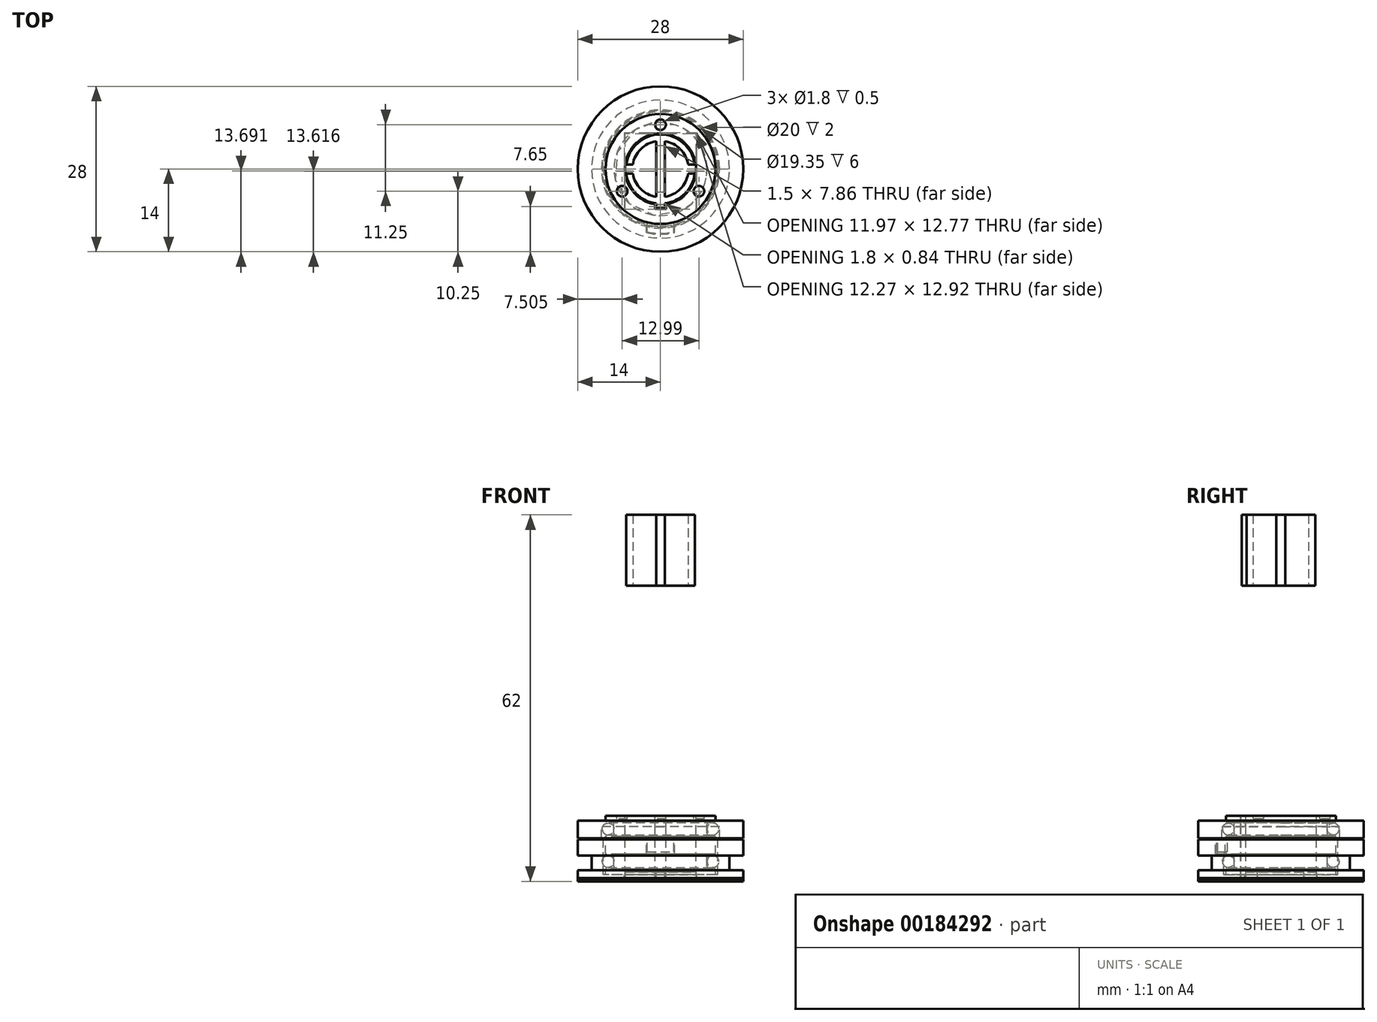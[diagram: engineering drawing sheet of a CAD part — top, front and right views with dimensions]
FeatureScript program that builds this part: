
annotation { "Feature Type Name" : "Feature", "Feature Type Description" : "" }
export const myFeature = defineFeature(function(context is Context, id is Id, definition is map)
    precondition{}
    {
        {
            assignVariable(context, id + "F0", {"name" : "fitT", "anyValue" : .15});
        }
        {
            assignVariable(context, id + "F1", {"name" : "slitWidth", "anyValue" : 1.5});
        }
        {
            assignVariable(context, id + "F2", {"name" : "topTierThick", "anyValue" : 1});
        }
        {
            assignVariable(context, id + "F3", {"name" : "bottomTierThick", "anyValue" : .55});
        }
        {
            assignVariable(context, id + "F4", {"name" : "bottomRingWall", "anyValue" : 6});
        }
        {
            assignVariable(context, id + "F5", {"name" : "oRingDiameter", "anyValue" : 2});
        }
        {
            assignVariable(context, id + "F6", {"name" : "ccThick", "anyValue" : 12});
        }
        {
            var Q0;
            Q0=qCreatedBy(makeId("Top.planeOp"),FACE);
            var sketch = newSketch(context, id + "F7", { "sketchPlane" : qUnion([Q0])});
            skCircle(sketch, "E0", {"center": v(0, 0) * mm, "radius": 14 * mm});
            skSolve(sketch);
        }
        {
            var Q0;
            Q0=makeQuery(id+"F7.imprint","IMPRINT",FACE,{"disambiguationData":[TD([[makeQuery(id+"F7.imprint","IMPRINT",EDGE,{"derivedFrom":sQuery(id+"F7.wireOp",EDGE,"E0")}),1.0]])]});
            extrude(context, id + "F8", {"entities" : qUnion([Q0]), "depth" : (getVariable(context, 'bottomTierThick')) * mm});
        }
        {
            var Q0;
            Q0=makeQuery(id+"F8.opExtrude","CAP_FACE",FACE,{"disambiguationData":[OSD([sQuery(id+"F7.wireOp",EDGE,"E0")])],"isStart":false});
            var sketch = newSketch(context, id + "F9", { "sketchPlane" : qUnion([Q0])});
            skArc(sketch, "E1", {"start": v(0.6, -5.97) * mm, "mid": v(0, 6) * mm, "end": v(-0.6, -5.97) * mm});
            skLineSegment(sketch, "E2", {"start": v(0, 0) * mm, "end": v(0, -14) * mm, "construction": true});
            skLineSegment(sketch, "E3.bottom", {"start": v(0.6, -6.6) * mm, "end": v(-0.6, -6.6) * mm});
            skLineSegment(sketch, "E3.left", {"start": v(0.6, -6.6) * mm, "end": v(0.6, -5.97) * mm});
            skLineSegment(sketch, "E3.right", {"start": v(-0.6, -6.6) * mm, "end": v(-0.6, -5.97) * mm});
            skPoint(sketch, "E3.middle", {"position": v(0, -6) * mm});
            skLineSegment(sketch, "E4", {"start": v(-2.04, -6) * mm, "end": v(2.09, -6) * mm, "construction": true});
            skSolve(sketch);
        }
        {
            var Q0;
            Q0=makeQuery(id+"F9.imprint","IMPRINT",FACE,{"disambiguationData":[TD([[makeQuery(id+"F9.imprint","IMPRINT",EDGE,{"derivedFrom":sQuery(id+"F9.wireOp",EDGE,"E1")}),1.0]])]});
            extrude(context, id + "F10", {"entities" : qUnion([Q0]), "operationType" : NewBodyOperationType.ADD, "depth" : (getVariable(context, 'topTierThick')) * mm});
        }
        {
            var Q0;
            Q0=makeQuery(id+"F10.opExtrude","CAP_FACE",FACE,{"disambiguationData":[OSD([sQuery(id+"F9.wireOp",EDGE,"E1")])],"isStart":false});
            var sketch = newSketch(context, id + "F11", { "sketchPlane" : qUnion([Q0])});
            skPoint(sketch, "E5.rect.middle", {"position": v(0, 0) * mm});
            skCircle(sketch, "E6", {"center": v(0, 0) * mm, "radius": 4 * mm, "construction": true});
            skLineSegment(sketch, "E7.rect.bottom", {"start": v(0.75, 3.93) * mm, "end": v(-0.75, 3.93) * mm});
            skLineSegment(sketch, "E7.rect.top", {"start": v(0.75, -3.93) * mm, "end": v(-0.75, -3.93) * mm});
            skLineSegment(sketch, "E7.rect.left", {"start": v(0.75, 3.93) * mm, "end": v(0.75, -3.93) * mm});
            skLineSegment(sketch, "E7.rect.right", {"start": v(-0.75, 3.93) * mm, "end": v(-0.75, -3.93) * mm});
            skSolve(sketch);
        }
        {
            var Q0;
            Q0=makeQuery(id+"F11.imprint","IMPRINT",FACE,{"disambiguationData":[TD([[makeQuery(id+"F11.imprint","IMPRINT",EDGE,{"derivedFrom":sQuery(id+"F11.wireOp",EDGE,"E7.rect.bottom")}),1.0]])]});
            var Q1;
            Q1=makeQuery(id+"F8.opExtrude","CAP_FACE",FACE,{"disambiguationData":[OSD([sQuery(id+"F7.wireOp",EDGE,"E0")])],"isStart":true});
            extrude(context, id + "F12", {"entities" : qUnion([Q0]), "operationType" : NewBodyOperationType.REMOVE, "endBound" : BoundingType.UP_TO_SURFACE, "oppositeDirection" : true, "endBoundEntityFace" : qUnion([Q1]), "depth" : 25 * mm});
        }
        {
            var Q0;
            Q0=qCreatedBy(makeId("Front.planeOp"),FACE);
            var sketch = newSketch(context, id + "F13", { "sketchPlane" : qUnion([Q0])});
            skLineSegment(sketch, "E8.bottom", {"start": v(-14, 7.1) * mm, "end": v(-9.67, 7.1) * mm});
            skLineSegment(sketch, "E8.top", {"start": v(-14, 0.1) * mm, "end": v(-9.67, 0.1) * mm});
            skLineSegment(sketch, "E8.left", {"start": v(-14, 7.1) * mm, "end": v(-14, 4.35) * mm});
            skLineSegment(sketch, "E8.right", {"start": v(-9.67, 7.1) * mm, "end": v(-9.67, 1.1) * mm});
            skLineSegment(sketch, "E9.bottom", {"start": v(-9.67, 1.1) * mm, "end": v(-6.15, 1.1) * mm});
            skLineSegment(sketch, "E9.top", {"start": v(-14, 0.1) * mm, "end": v(-6.15, 0.1) * mm});
            skLineSegment(sketch, "E9.left", {"start": v(-14, 1.1) * mm, "end": v(-14, 0.1) * mm});
            skLineSegment(sketch, "E9.right", {"start": v(-6.15, 1.1) * mm, "end": v(-6.15, 0.1) * mm});
            skLineSegment(sketch, "E10", {"start": v(0, 8.92) * mm, "end": v(0, -8.7) * mm, "construction": true});
            skLineSegment(sketch, "E11", {"start": v(-12.77, 0) * mm, "end": v(12.68, 0) * mm, "construction": true});
            skLineSegment(sketch, "E12.bottom", {"start": v(-14, 4.35) * mm, "end": v(-11.67, 4.35) * mm});
            skLineSegment(sketch, "E12.top", {"start": v(-14, 1.85) * mm, "end": v(-11.67, 1.85) * mm});
            skLineSegment(sketch, "E12.right", {"start": v(-11.67, 4.35) * mm, "end": v(-11.67, 1.85) * mm});
            skLineSegment(sketch, "E13.trimOffspring", {"start": v(-14, 1.85) * mm, "end": v(-14, 0.1) * mm});
            skSolve(sketch);
        }
        {
            var Q0;
            Q0=makeQuery(id+"F13.imprint","IMPRINT",FACE,{"disambiguationData":[TD([[makeQuery(id+"F13.imprint","IMPRINT",EDGE,{"derivedFrom":sQuery(id+"F13.wireOp",EDGE,"E8.bottom")}),-1.0]])]});
            var Q1;
            Q1=sQuery(id+"F13.wireOp",EDGE,"E10");
            revolve(context, id + "F14", {"entities" : qUnion([Q0]), "axis" : qUnion([Q1]), "revolveType" : RevolveType.FULL});
        }
        {
            var Q0;
            Q0=qCreatedBy(makeId("Front.planeOp"),FACE);
            var sketch = newSketch(context, id + "F15", { "sketchPlane" : qUnion([Q0])});
            skLineSegment(sketch, "E14.bottom", {"start": v(-14, 10.25) * mm, "end": v(0, 10.25) * mm});
            skLineSegment(sketch, "E14.top", {"start": v(-14, 7.25) * mm, "end": v(-10, 7.25) * mm});
            skLineSegment(sketch, "E14.left", {"start": v(-14, 10.25) * mm, "end": v(-14, 7.25) * mm});
            skLineSegment(sketch, "E14.right", {"start": v(0, 10.25) * mm, "end": v(0, 9.25) * mm});
            skLineSegment(sketch, "E15.top", {"start": v(-10, 9.25) * mm, "end": v(0, 9.25) * mm});
            skLineSegment(sketch, "E15.left", {"start": v(-10, 7.25) * mm, "end": v(-10, 9.25) * mm});
            skSolve(sketch);
        }
        {
            var Q0;
            Q0=makeQuery(id+"F15.imprint","IMPRINT",FACE,{"disambiguationData":[TD([[makeQuery(id+"F15.imprint","IMPRINT",EDGE,{"derivedFrom":sQuery(id+"F15.wireOp",EDGE,"E14.bottom")}),-1.0]])]});
            var Q1;
            Q1=sQuery(id+"F13.wireOp",EDGE,"E10");
            revolve(context, id + "F16", {"entities" : qUnion([Q0]), "axis" : qUnion([Q1]), "revolveType" : RevolveType.FULL});
        }
        {
            var Q0;
            Q0=qCreatedBy(makeId("Top.planeOp"),FACE);
            cPlane(context, id + "F17", {"entities" : qUnion([Q0]), "cplaneType" : CPlaneType.OFFSET, "offset" : 50 * mm, "width" : 150 * mm, "height" : 150 * mm});
        }
        {
            var Q0;
            Q0=qCreatedBy(id+"F17.planeOp",FACE);
            var sketch = newSketch(context, id + "F18", { "sketchPlane" : qUnion([Q0])});
            skArc(sketch, "E16", {"start": v(-5.8, -0.75) * mm, "mid": v(0, -5.85) * mm, "end": v(5.8, -0.75) * mm});
            skArc(sketch, "E17", {"start": v(4.7, 0.75) * mm, "mid": v(3.36, 3.36) * mm, "end": v(0.75, 4.7) * mm});
            skLineSegment(sketch, "E18.left", {"start": v(-0.75, 4.7) * mm, "end": v(-0.75, -4.7) * mm});
            skLineSegment(sketch, "E18.right", {"start": v(0.75, 4.7) * mm, "end": v(0.75, -4.7) * mm});
            skLineSegment(sketch, "E19.bottom", {"start": v(-5.8, 0.75) * mm, "end": v(-4.7, 0.75) * mm});
            skLineSegment(sketch, "E19.top", {"start": v(-5.8, -0.75) * mm, "end": v(-4.7, -0.75) * mm});
            skArc(sketch, "E20.trimOffspring", {"start": v(5.8, 0.75) * mm, "mid": v(0, 5.85) * mm, "end": v(-5.8, 0.75) * mm});
            skArc(sketch, "E21.trimOffspring", {"start": v(-4.7, -0.75) * mm, "mid": v(-3.36, -3.36) * mm, "end": v(-0.75, -4.7) * mm});
            skLineSegment(sketch, "E22.trimOffspring", {"start": v(4.7, 0.75) * mm, "end": v(5.8, 0.75) * mm});
            skArc(sketch, "E23.trimOffspring", {"start": v(-0.75, 4.7) * mm, "mid": v(-3.36, 3.36) * mm, "end": v(-4.7, 0.75) * mm});
            skLineSegment(sketch, "E24.trimOffspring", {"start": v(4.7, -0.75) * mm, "end": v(5.8, -0.75) * mm});
            skArc(sketch, "E25.trimOffspring", {"start": v(0.75, -4.7) * mm, "mid": v(3.36, -3.36) * mm, "end": v(4.7, -0.75) * mm});
            skSolve(sketch);
        }
        {
            var Q0;
            Q0=qSketchRegion(id+"F18",true);
            extrude(context, id + "F19", {"entities" : qUnion([Q0]), "depth" : (getVariable(context, 'ccThick')) * mm});
        }
        {
            var Q0;
            Q0=qCreatedBy(makeId("Front.planeOp"),FACE);
            var sketch = newSketch(context, id + "F20", { "sketchPlane" : qUnion([Q0])});
            skLineSegment(sketch, "E26.bottom", {"start": v(-9.3, 11.1) * mm, "end": v(-6, 11.1) * mm});
            skLineSegment(sketch, "E26.top", {"start": v(-9.3, 1.1) * mm, "end": v(-6, 1.1) * mm});
            skLineSegment(sketch, "E26.left", {"start": v(-9.3, 11.1) * mm, "end": v(-9.3, 10.1) * mm});
            skLineSegment(sketch, "E26.right", {"start": v(-6, 11.1) * mm, "end": v(-6, 1.1) * mm});
            skLineSegment(sketch, "E27.bottom", {"start": v(-9.3, 4.6) * mm, "end": v(-8.38, 4.6) * mm});
            skLineSegment(sketch, "E27.top", {"start": v(-9.3, 2.1) * mm, "end": v(-8.38, 2.1) * mm});
            skLineSegment(sketch, "E27.right", {"start": v(-7.87, 4.1) * mm, "end": v(-7.87, 2.6) * mm});
            skLineSegment(sketch, "E28.bottom", {"start": v(-9.3, 10.1) * mm, "end": v(-8.38, 10.1) * mm});
            skLineSegment(sketch, "E28.top", {"start": v(-9.3, 7.6) * mm, "end": v(-8.38, 7.6) * mm});
            skLineSegment(sketch, "E28.right", {"start": v(-7.88, 9.6) * mm, "end": v(-7.88, 8.1) * mm});
            skLineSegment(sketch, "E29.trimOffspring", {"start": v(-9.3, 7.6) * mm, "end": v(-9.3, 4.6) * mm});
            skLineSegment(sketch, "E30.trimOffspring", {"start": v(-9.3, 2.1) * mm, "end": v(-9.3, 1.1) * mm});
            skPoint(sketch, "E31.visualSharp", {"position": v(-7.88, 10.1) * mm});
            skArc(sketch, "E31.filletArc", {"start": v(-7.88, 9.6) * mm, "mid": v(-8.02, 9.95) * mm, "end": v(-8.38, 10.1) * mm});
            skPoint(sketch, "E32.visualSharp", {"position": v(-7.88, 7.6) * mm});
            skArc(sketch, "E32.filletArc", {"start": v(-8.38, 7.6) * mm, "mid": v(-8.02, 7.75) * mm, "end": v(-7.88, 8.1) * mm});
            skPoint(sketch, "E33.visualSharp", {"position": v(-7.88, 4.6) * mm});
            skArc(sketch, "E33.filletArc", {"start": v(-7.88, 4.1) * mm, "mid": v(-8.02, 4.45) * mm, "end": v(-8.38, 4.6) * mm});
            skPoint(sketch, "E34.visualSharp", {"position": v(-7.88, 2.1) * mm});
            skArc(sketch, "E34.filletArc", {"start": v(-8.38, 2.1) * mm, "mid": v(-8.02, 2.25) * mm, "end": v(-7.88, 2.6) * mm});
            skLineSegment(sketch, "E35", {"start": v(-7.88, 8.1) * mm, "end": v(-7.88, 4.1) * mm, "construction": true});
            skPoint(sketch, "E36", {"position": v(-7.88, 8.85) * mm});
            skPoint(sketch, "E37", {"position": v(-7.88, 3.35) * mm});
            skCircle(sketch, "E38", {"center": v(-8.88, 3.35) * mm, "radius": 1 * mm});
            skCircle(sketch, "E39", {"center": v(-8.88, 8.85) * mm, "radius": 1 * mm});
            skLineSegment(sketch, "E40", {"start": v(0, 21.5) * mm, "end": v(0, -11.55) * mm, "construction": true});
            skSolve(sketch);
        }
        {
            var Q0;
            Q0=makeQuery(id+"F20.imprint","IMPRINT",FACE,{"disambiguationData":[TD([[makeQuery(id+"F20.imprint","IMPRINT",EDGE,{"derivedFrom":sQuery(id+"F20.wireOp",EDGE,"E26.bottom")}),-1.0]])]});
            var Q1;
            Q1=sQuery(id+"F20.wireOp",EDGE,"E40");
            revolve(context, id + "F21", {"entities" : qUnion([Q0]), "axis" : qUnion([Q1]), "revolveType" : RevolveType.FULL});
        }
        {
            var Q0;
            Q0=makeQuery(id+"F20.imprint","IMPRINT",FACE,{"disambiguationData":[TD([[makeQuery(id+"F20.imprint","IMPRINT",EDGE,{"derivedFrom":sQuery(id+"F20.wireOp",EDGE,"E39")}),1.0]])]});
            var Q1;
            Q1=makeQuery(id+"F20.imprint","IMPRINT",FACE,{"disambiguationData":[TD([[makeQuery(id+"F20.imprint","IMPRINT",EDGE,{"derivedFrom":sQuery(id+"F20.wireOp",EDGE,"E38")}),1.0]])]});
            var Q2;
            Q2=sQuery(id+"F20.wireOp",EDGE,"E40");
            revolve(context, id + "F22", {"entities" : qUnion([Q0, Q1]), "axis" : qUnion([Q2]), "revolveType" : RevolveType.FULL});
        }
        {
            var Q0;
            Q0=makeQuery(id+"F14.opRevolve","SWEPT_FACE",FACE,{"disambiguationData":[OSD([sQuery(id+"F13.wireOp",EDGE,"E8.bottom")])]});
            var sketch = newSketch(context, id + "F23", { "sketchPlane" : qUnion([Q0])});
            skLineSegment(sketch, "E41", {"start": v(0, 14) * mm, "end": v(0, -14) * mm, "construction": true});
            skLineSegment(sketch, "E42", {"start": v(0, -14) * mm, "end": v(14, 0) * mm, "construction": true});
            skLineSegment(sketch, "E43", {"start": v(14, 0) * mm, "end": v(-14, 0) * mm, "construction": true});
            skLineSegment(sketch, "E44", {"start": v(-14, 0) * mm, "end": v(0, -14) * mm, "construction": true});
            skLineSegment(sketch, "E45", {"start": v(0, 14) * mm, "end": v(-14, 0) * mm, "construction": true});
            skLineSegment(sketch, "E46", {"start": v(14, 0) * mm, "end": v(0, 14) * mm, "construction": true});
            skLineSegment(sketch, "E47.left", {"start": v(2.4, -10.76) * mm, "end": v(2.4, -9.37) * mm});
            skLineSegment(sketch, "E47.right", {"start": v(-2.4, -10.76) * mm, "end": v(-2.4, -9.37) * mm});
            skPoint(sketch, "E47.middle", {"position": v(0, -7.24) * mm});
            skArc(sketch, "E48", {"start": v(-2.4, -9.37) * mm, "mid": v(0, -9.68) * mm, "end": v(2.4, -9.37) * mm});
            skPoint(sketch, "E49.orphan", {"position": v(2.4, -3.72) * mm});
            skPoint(sketch, "E47.top.end.orphan", {"position": v(-2.4, -3.72) * mm});
            skArc(sketch, "E50", {"start": v(-2.4, -10.76) * mm, "mid": v(0, -11.03) * mm, "end": v(2.4, -10.76) * mm});
            skSolve(sketch);
        }
        {
            var Q0;
            Q0=makeQuery(id+"F23.imprint","IMPRINT",FACE,{"disambiguationData":[TD([[makeQuery(id+"F23.imprint","IMPRINT",EDGE,{"derivedFrom":sQuery(id+"F23.wireOp",EDGE,"E47.left")}),1.0]])]});
            extrude(context, id + "F24", {"entities" : qUnion([Q0]), "operationType" : NewBodyOperationType.REMOVE, "oppositeDirection" : true, "depth" : (3 / 2 * getVariable(context, 'slitWidth') + getVariable(context, 'fitT')) * mm});
        }
        {
            var Q0;
            Q0=makeQuery(id+"F14.opRevolve","SWEPT_FACE",FACE,{"disambiguationData":[OSD([sQuery(id+"F13.wireOp",EDGE,"E8.bottom")])]});
            var sketch = newSketch(context, id + "F25", { "sketchPlane" : qUnion([Q0])});
            skArc(sketch, "E51", {"start": v(-2.25, -10.64) * mm, "mid": v(0, -10.88) * mm, "end": v(2.25, -10.64) * mm});
            skLineSegment(sketch, "E52", {"start": v(10.42, 0) * mm, "end": v(-10.42, 0) * mm, "construction": true});
            skLineSegment(sketch, "E53", {"start": v(0, -10.88) * mm, "end": v(0, 10.88) * mm, "construction": true});
            skPoint(sketch, "E53.endSnap0", {"position": v(0, 9.67) * mm});
            skLineSegment(sketch, "E54.left", {"start": v(2.25, -10.64) * mm, "end": v(2.25, -5.56) * mm});
            skLineSegment(sketch, "E54.right", {"start": v(-2.25, -10.64) * mm, "end": v(-2.25, -5.56) * mm});
            skPoint(sketch, "E54.middle", {"position": v(0, -7.65) * mm});
            skArc(sketch, "E55", {"start": v(-2.25, -5.56) * mm, "mid": v(0, -6) * mm, "end": v(2.25, -5.56) * mm});
            skPoint(sketch, "E56.orphan", {"position": v(2.25, -4.67) * mm});
            skPoint(sketch, "E57.orphan", {"position": v(-2.25, -4.67) * mm});
            skSolve(sketch);
        }
        {
            var Q0;
            {var subQ1=sQuery(id+"F25.wireOp",EDGE,"E51");Q0=makeQuery(id+"F25.imprint","IMPRINT",FACE,{"disambiguationData":[TD([[makeQuery(id+"F25.imprint","IMPRINT",EDGE,{"derivedFrom":subQ1}),1.0]])]});}
            var Q1;
            {var subQ0=sQuery(id+"F25.wireOp",EDGE,"E55");Q1=makeQuery(id+"F25.imprint","IMPRINT",FACE,{"disambiguationData":[TD([[makeQuery(id+"F25.imprint","IMPRINT",EDGE,{"derivedFrom":subQ0}),-1.0]])]});}
            extrude(context, id + "F26", {"entities" : qUnion([Q0, Q1]), "operationType" : NewBodyOperationType.ADD, "oppositeDirection" : true, "depth" : (3 / 2 * getVariable(context, 'slitWidth') - getVariable(context, 'fitT')) * mm});
        }
        {
            var Q0;
            Q0=makeQuery(id+"F21.opRevolve","SWEPT_FACE",FACE,{"disambiguationData":[OSD([sQuery(id+"F20.wireOp",EDGE,"E26.bottom")])]});
            var sketch = newSketch(context, id + "F27", { "sketchPlane" : qUnion([Q0])});
            skLineSegment(sketch, "E58", {"start": v(0, 9.3) * mm, "end": v(0, -9.3) * mm, "construction": true});
            skLineSegment(sketch, "E59", {"start": v(0, -9.3) * mm, "end": v(9.3, 0) * mm, "construction": true});
            skLineSegment(sketch, "E60", {"start": v(9.3, 0) * mm, "end": v(-9.3, 0) * mm, "construction": true});
            skLineSegment(sketch, "E61", {"start": v(-9.3, 0) * mm, "end": v(0, 9.3) * mm, "construction": true});
            skLineSegment(sketch, "E62", {"start": v(0, 9.3) * mm, "end": v(9.3, 0) * mm, "construction": true});
            skLineSegment(sketch, "E63", {"start": v(0, -9.3) * mm, "end": v(-9.3, 0) * mm, "construction": true});
            skLineSegment(sketch, "E64.bottom", {"start": v(0.9, -6.77) * mm, "end": v(-0.9, -6.73) * mm});
            skLineSegment(sketch, "E64.left", {"start": v(0.9, -6.77) * mm, "end": v(0.9, -5.93) * mm});
            skLineSegment(sketch, "E64.right", {"start": v(-0.9, -6.73) * mm, "end": v(-0.9, -5.93) * mm});
            skPoint(sketch, "E64.middle", {"position": v(0, -6) * mm});
            skArc(sketch, "E65", {"start": v(-0.9, -5.93) * mm, "mid": v(0, -6) * mm, "end": v(0.9, -5.93) * mm});
            skPoint(sketch, "E66.orphan", {"position": v(-0.9, -5.23) * mm});
            skPoint(sketch, "E67.orphan", {"position": v(0.9, -5.27) * mm});
            skLineSegment(sketch, "E68", {"start": v(-3.37, -5.93) * mm, "end": v(3.24, -6.07) * mm, "construction": true});
            skSolve(sketch);
        }
        {
            var Q0;
            Q0=makeQuery(id+"F27.imprint","IMPRINT",FACE,{"disambiguationData":[TD([[makeQuery(id+"F27.imprint","IMPRINT",EDGE,{"derivedFrom":sQuery(id+"F27.wireOp",EDGE,"E64.bottom")}),-1.0]])]});
            var Q1;
            Q1=makeQuery(id+"F14.opRevolve","SWEPT_FACE",FACE,{"disambiguationData":[OSD([sQuery(id+"F13.wireOp",EDGE,"E9.top")])]});
            extrude(context, id + "F28", {"entities" : qUnion([Q0]), "operationType" : NewBodyOperationType.REMOVE, "endBound" : BoundingType.UP_TO_SURFACE, "oppositeDirection" : true, "endBoundEntityFace" : qUnion([Q1]), "depth" : (getVariable(context, 'bottomRingWall') + 2 * getVariable(context, 'oRingDiameter')) * mm});
        }
        {
            var Q0;
            Q0=makeQuery(id+"F19.opExtrude","CAP_FACE",FACE,{"disambiguationData":[OSD([sQuery(id+"F18.wireOp",EDGE,"E16"),sQuery(id+"F18.wireOp",EDGE,"E17"),sQuery(id+"F18.wireOp",EDGE,"E18.left"),sQuery(id+"F18.wireOp",EDGE,"E18.right"),sQuery(id+"F18.wireOp",EDGE,"E19.bottom"),sQuery(id+"F18.wireOp",EDGE,"E19.top"),sQuery(id+"F18.wireOp",EDGE,"E20.trimOffspring"),sQuery(id+"F18.wireOp",EDGE,"E21.trimOffspring"),sQuery(id+"F18.wireOp",EDGE,"E22.trimOffspring"),sQuery(id+"F18.wireOp",EDGE,"E23.trimOffspring"),sQuery(id+"F18.wireOp",EDGE,"E24.trimOffspring"),sQuery(id+"F18.wireOp",EDGE,"E25.trimOffspring")])],"isStart":false});
            var sketch = newSketch(context, id + "F29", { "sketchPlane" : qUnion([Q0])});
            skLineSegment(sketch, "E69", {"start": v(0, 5.85) * mm, "end": v(0, -5.85) * mm, "construction": true});
            skLineSegment(sketch, "E70", {"start": v(0, -5.85) * mm, "end": v(5.8, 0) * mm, "construction": true});
            skLineSegment(sketch, "E71", {"start": v(5.8, 0) * mm, "end": v(-5.8, 0) * mm, "construction": true});
            skLineSegment(sketch, "E72", {"start": v(-5.8, 0) * mm, "end": v(0, 5.85) * mm, "construction": true});
            skLineSegment(sketch, "E73", {"start": v(5.8, 0) * mm, "end": v(0, 5.85) * mm, "construction": true});
            skLineSegment(sketch, "E74", {"start": v(0, -5.85) * mm, "end": v(-5.8, 0) * mm, "construction": true});
            skLineSegment(sketch, "E75.bottom", {"start": v(0.75, -6.6) * mm, "end": v(-0.75, -6.6) * mm});
            skLineSegment(sketch, "E75.top", {"start": v(0.75, -5.1) * mm, "end": v(-0.75, -5.1) * mm});
            skLineSegment(sketch, "E75.left", {"start": v(0.75, -6.6) * mm, "end": v(0.75, -5.1) * mm});
            skLineSegment(sketch, "E75.right", {"start": v(-0.75, -6.6) * mm, "end": v(-0.75, -5.1) * mm});
            skPoint(sketch, "E75.middle", {"position": v(0, -5.85) * mm});
            skSolve(sketch);
        }
        {
            var Q0;
            {var subQ0=sQuery(id+"F29.wireOp",EDGE,"E75.bottom");Q0=makeQuery(id+"F29.imprint","IMPRINT",FACE,{"disambiguationData":[TD([[makeQuery(id+"F29.imprint","IMPRINT",EDGE,{"derivedFrom":subQ0}),-1.0]])]});}
            extrude(context, id + "F30", {"entities" : qUnion([Q0]), "operationType" : NewBodyOperationType.ADD, "oppositeDirection" : true, "depth" : (getVariable(context, 'ccThick')) * mm});
        }
        {
            var Q0;
            Q0=makeQuery(id+"F21.opRevolve","SWEPT_FACE",FACE,{"disambiguationData":[OSD([sQuery(id+"F20.wireOp",EDGE,"E26.bottom")])]});
            var sketch = newSketch(context, id + "F31", { "sketchPlane" : qUnion([Q0])});
            skCircle(sketch, "E76", {"center": v(0, 7.5) * mm, "radius": 0.9 * mm});
            skPoint(sketch, "E76.centerSnap0", {"position": v(0, 6) * mm});
            skCircle(sketch, "E77.1.0", {"center": v(6.5, -3.75) * mm, "radius": 0.9 * mm});
            skCircle(sketch, "E77.2.0", {"center": v(-6.5, -3.75) * mm, "radius": 0.9 * mm});
            skPoint(sketch, "E77.center", {"position": v(0, 0) * mm});
            skLineSegment(sketch, "E77.anchor1", {"start": v(0, 0) * mm, "end": v(0, 7.5) * mm, "construction": true});
            skLineSegment(sketch, "E77.anchor2", {"start": v(0, 0) * mm, "end": v(-6.5, -3.75) * mm, "construction": true});
            skSolve(sketch);
        }
        {
            var Q0;
            Q0=makeQuery(id+"F31.imprint","IMPRINT",FACE,{"disambiguationData":[TD([[makeQuery(id+"F31.imprint","IMPRINT",EDGE,{"derivedFrom":sQuery(id+"F31.wireOp",EDGE,"E76")}),1.0]])]});
            var Q1;
            Q1=makeQuery(id+"F31.imprint","IMPRINT",FACE,{"disambiguationData":[TD([[makeQuery(id+"F31.imprint","IMPRINT",EDGE,{"derivedFrom":sQuery(id+"F31.wireOp",EDGE,"E77.1.0")}),1.0]])]});
            var Q2;
            Q2=makeQuery(id+"F31.imprint","IMPRINT",FACE,{"disambiguationData":[TD([[makeQuery(id+"F31.imprint","IMPRINT",EDGE,{"derivedFrom":sQuery(id+"F31.wireOp",EDGE,"E77.2.0")}),1.0]])]});
            extrude(context, id + "F32", {"entities" : qUnion([Q0, Q1, Q2]), "operationType" : NewBodyOperationType.REMOVE, "oppositeDirection" : true, "depth" : .5 * mm});
        }
    });
